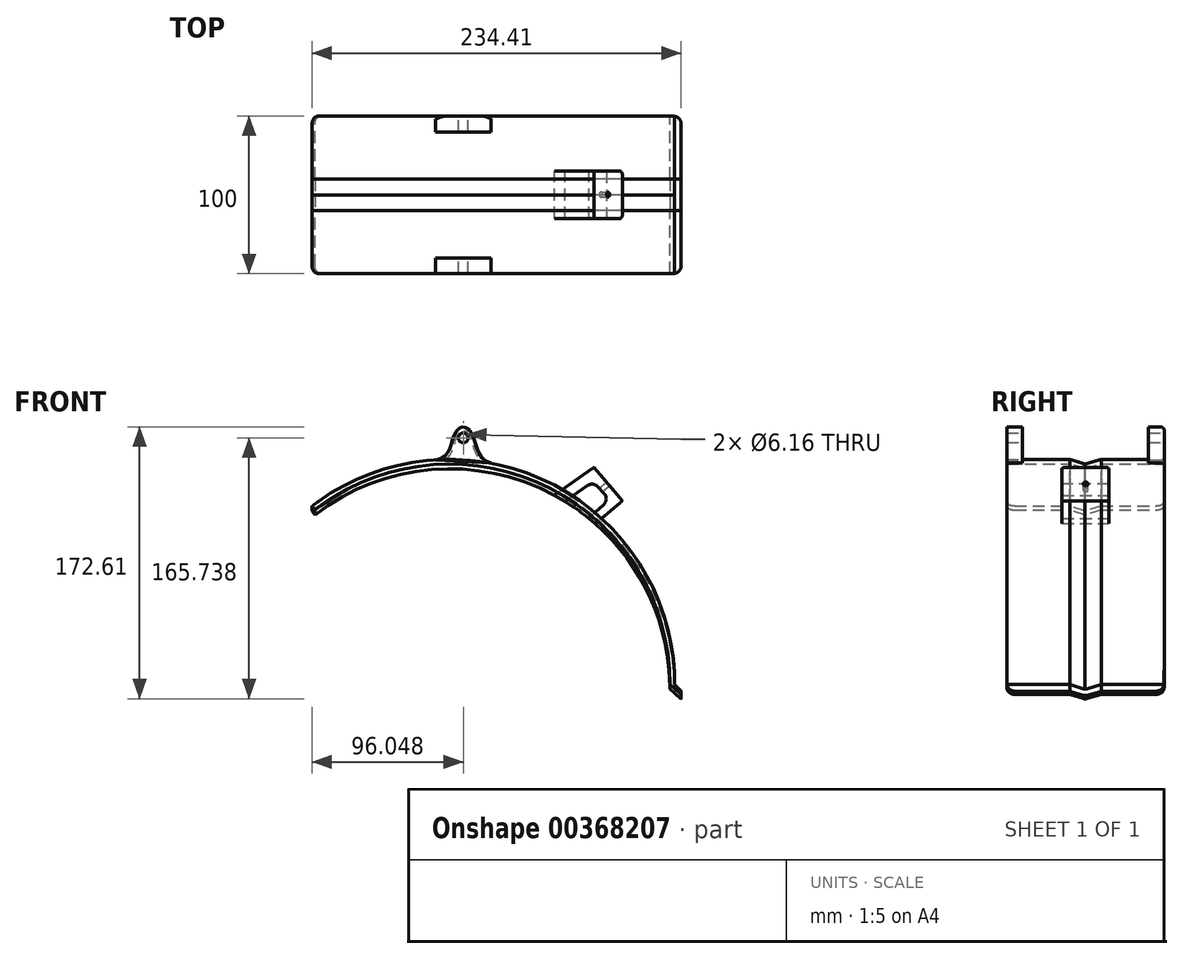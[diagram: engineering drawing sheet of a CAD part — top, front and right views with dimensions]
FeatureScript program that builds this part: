
annotation { "Feature Type Name" : "Feature", "Feature Type Description" : "" }
export const myFeature = defineFeature(function(context is Context, id is Id, definition is map)
    precondition{}
    {
        {
            var Q0;
            Q0=qCreatedBy(makeId("Front.planeOp"),FACE);
            var sketch = newSketch(context, id + "F0", { "sketchPlane" : qUnion([Q0])});
            skArc(sketch, "E0", {"start": v(134.32, 0) * mm, "mid": v(-8.68, 143) * mm, "end": v(-151.68, 0) * mm});
            skArc(sketch, "E1", {"start": v(131.32, 0) * mm, "mid": v(-8.68, 140) * mm, "end": v(-148.68, 0) * mm});
            skLineSegment(sketch, "E2", {"start": v(131.32, 0) * mm, "end": v(134.32, 0) * mm});
            skLineSegment(sketch, "E3", {"start": v(131.32, 0) * mm, "end": v(138.4, -6.25) * mm});
            skLineSegment(sketch, "E4", {"start": v(138.4, -6.25) * mm, "end": v(138.4, -4.25) * mm});
            skLineSegment(sketch, "E5", {"start": v(134.32, 0) * mm, "end": v(138.4, -4.25) * mm});
            skLineSegment(sketch, "E6", {"start": v(-96.01, 113.24) * mm, "end": v(-94.22, 110.83) * mm});
            skSolve(sketch);
        }
        {
            var Q0;
            Q0 = qSketchRegion(id + "F0", true);
            extrude(context, id + "F1", {"entities" : qUnion([Q0]), "depth" : 40 * mm});
        }
        {
            var Q0;
            Q0=qCreatedBy(makeId("Right.planeOp"),FACE);
            var sketch = newSketch(context, id + "F2", { "sketchPlane" : qUnion([Q0])});
            skLineSegment(sketch, "E7", {"start": v(-40, 0) * mm, "end": v(-50.26, -3) * mm});
            skLineSegment(sketch, "E8", {"start": v(-50.26, -3) * mm, "end": v(-60, 0) * mm});
            skSolve(sketch);
        }
        {
            var Q0;
            Q0=makeQuery(id+"F1.opExtrude","CAP_FACE",FACE,{"disambiguationData":[OSD([sQuery(id+"F0.wireOp",EDGE,"E0"),sQuery(id+"F0.wireOp",EDGE,"E1"),sQuery(id+"F0.wireOp",EDGE,"rE3FSKzE-tdSS-Yi37-PZmk-w9ympNAeDIpR"),sQuery(id+"F0.wireOp",EDGE,"E3"),sQuery(id+"F0.wireOp",EDGE,"E4"),sQuery(id+"F0.wireOp",EDGE,"E5")])],"isStart":false});
            var Q1;
            Q1=sQuery(id+"F2.wireOp",EDGE,"E7");
            sweep(context, id + "F3", {"profiles" : qUnion([Q0]), "path" : qUnion([Q1])});
        }
        {
            var Q0;
            Q0=makeQuery(id+"F3.opSweep","CAP_FACE",FACE,{"disambiguationData":[OSD([sQuery(id+"F0.wireOp",EDGE,"E0"),sQuery(id+"F0.wireOp",EDGE,"E1"),sQuery(id+"F0.wireOp",EDGE,"rE3FSKzE-tdSS-Yi37-PZmk-w9ympNAeDIpR"),sQuery(id+"F0.wireOp",EDGE,"E3"),sQuery(id+"F0.wireOp",EDGE,"E4"),sQuery(id+"F0.wireOp",EDGE,"E5"),sQuery(id+"F2.wireOp",VERTEX,"E7.end")])],"isStart":false});
            var Q1;
            Q1=sQuery(id+"F2.wireOp",EDGE,"E8");
            sweep(context, id + "F4", {"operationType" : NewBodyOperationType.ADD, "profiles" : qUnion([Q0]), "path" : qUnion([Q1])});
        }
        {
            var Q0;
            Q0=makeQuery(id+"F4.opSweep","CAP_FACE",FACE,{"disambiguationData":[OSD([sQuery(id+"F0.wireOp",EDGE,"E0"),sQuery(id+"F0.wireOp",EDGE,"E1"),sQuery(id+"F0.wireOp",EDGE,"rE3FSKzE-tdSS-Yi37-PZmk-w9ympNAeDIpR"),sQuery(id+"F0.wireOp",EDGE,"E3"),sQuery(id+"F0.wireOp",EDGE,"E4"),sQuery(id+"F0.wireOp",EDGE,"E5"),sQuery(id+"F2.wireOp",VERTEX,"E7.end"),sQuery(id+"F2.wireOp",VERTEX,"E8.end")])],"isStart":false});
            var Q1;
            Q1 = qSketchRegion(id + "F2", true);
            extrude(context, id + "F5", {"entities" : qUnion([Q0, Q1]), "operationType" : NewBodyOperationType.ADD, "depth" : 40 * mm});
        }
        {
            var Q0;
            Q0=qCreatedBy(makeId("Front.planeOp"),FACE);
            var sketch = newSketch(context, id + "F6", { "sketchPlane" : qUnion([Q0])});
            skFitSpline(sketch, "E9", {"points": [v(-17.5, 142.73) * mm, v(-5.94, 158) * mm, v(0, 163.52) * mm, v(6.18, 157.86) * mm, v(17.58, 140.57) * mm], "startDerivative": vector(93.4, 8.74) * mm, "endDerivative": vector(82.75, -24.1) * mm});
            skLineSegment(sketch, "E10", {"start": v(-17.5, 142.73) * mm, "end": v(17.58, 140.57) * mm});
            skLineSegment(sketch, "E11", {"start": v(0.04, 156.65) * mm, "end": v(0, 141.65) * mm});
            skPoint(sketch, "E11.startSnap0", {"position": v(0.04, 141.65) * mm});
            skCircle(sketch, "E12", {"center": v(0.04, 156.65) * mm, "radius": 3.08 * mm});
            skSolve(sketch);
        }
        {
            var Q0;
            Q0 = qSketchRegion(id + "F6", true);
            extrude(context, id + "F7", {"entities" : qUnion([Q0]), "operationType" : NewBodyOperationType.ADD, "depth" : 10 * mm});
        }
        {
            var Q0;
            Q0 = qSketchRegion(id + "F6", true);
            var Q1;
            Q1=makeQuery(id+"F5.opExtrude","CAP_FACE",FACE,{"disambiguationData":[OSD([sQuery(id+"F0.wireOp",EDGE,"E0"),sQuery(id+"F0.wireOp",EDGE,"E1"),sQuery(id+"F0.wireOp",EDGE,"E3"),sQuery(id+"F0.wireOp",EDGE,"E4"),sQuery(id+"F0.wireOp",EDGE,"E5"),sQuery(id+"F0.wireOp",EDGE,"E6"),sQuery(id+"F2.wireOp",VERTEX,"E7.end"),sQuery(id+"F2.wireOp",VERTEX,"E8.end")])],"isStart":false});
            extrude(context, id + "F8", {"entities" : qUnion([Q0]), "endBound" : BoundingType.UP_TO_SURFACE, "endBoundEntityFace" : qUnion([Q1]), "depth" : 99 * mm, "hasSecondDirection" : true, "secondDirectionOppositeDirection" : false, "secondDirectionDepth" : 90 * mm});
        }
        {
            var Q0;
            Q0=qCreatedBy(makeId("Front.planeOp"),FACE);
            var sketch = newSketch(context, id + "F9", { "sketchPlane" : qUnion([Q0])});
            skLineSegment(sketch, "E13", {"start": v(57.91, 120.15) * mm, "end": v(83.18, 137.94) * mm});
            skLineSegment(sketch, "E14", {"start": v(83.18, 137.94) * mm, "end": v(101.02, 116.66) * mm});
            skLineSegment(sketch, "E15", {"start": v(101.02, 116.66) * mm, "end": v(83.72, 102.17) * mm});
            skLineSegment(sketch, "E16", {"start": v(64.64, 116.26) * mm, "end": v(82.45, 128.8) * mm});
            skLineSegment(sketch, "E17", {"start": v(82.45, 128.8) * mm, "end": v(92.9, 117.86) * mm});
            skLineSegment(sketch, "E18", {"start": v(92.9, 117.86) * mm, "end": v(79.89, 105.42) * mm});
            skLineSegment(sketch, "E19", {"start": v(57.91, 120.15) * mm, "end": v(64.64, 116.26) * mm});
            skLineSegment(sketch, "E20", {"start": v(79.89, 105.42) * mm, "end": v(83.72, 102.17) * mm});
            skSolve(sketch);
        }
        {
            var Q0;
            Q0 = qSketchRegion(id + "F9", true);
            extrude(context, id + "F10", {"entities" : qUnion([Q0]), "depth" : 65 * mm, "hasSecondDirection" : true, "secondDirectionOppositeDirection" : false, "secondDirectionDepth" : 35 * mm});
        }
        {
            var Q0;
            Q0=makeQuery(id+"F10.opExtrude","CAP_EDGE",EDGE,{"disambiguationData":[OSD([sQuery(id+"F9.wireOp",EDGE,"E14")])],"isStart":false});
            var Q1;
            Q1=makeQuery(id+"F10.opExtrude","CAP_EDGE",EDGE,{"disambiguationData":[OSD([sQuery(id+"F9.wireOp",EDGE,"E14")])],"isStart":true});
            var Q2;
            Q2=makeQuery(id+"F7.opExtrude","CAP_EDGE",EDGE,{"disambiguationData":[OSD([sQuery(id+"F6.wireOp",EDGE,"E9")])],"isStart":true});
            var Q3;
            Q3=makeQuery(id+"F8.opExtrude","TWEAK_EDGE",EDGE,{"derivedFrom":[makeQuery(id+"F5.opExtrude","CAP_FACE",FACE,{"disambiguationData":[OSD([sQuery(id+"F0.wireOp",EDGE,"E0"),sQuery(id+"F0.wireOp",EDGE,"E1"),sQuery(id+"F0.wireOp",EDGE,"E3"),sQuery(id+"F0.wireOp",EDGE,"E4"),sQuery(id+"F0.wireOp",EDGE,"E5"),sQuery(id+"F0.wireOp",EDGE,"E6"),sQuery(id+"F2.wireOp",VERTEX,"E7.end"),sQuery(id+"F2.wireOp",VERTEX,"E8.end")])],"isStart":false}),makeQuery(id+"F6.imprint","IMPRINT",EDGE,{"derivedFrom":sQuery(id+"F6.wireOp",EDGE,"E9")})]});
            fillet(context, id + "F11", {"entities" : qUnion([Q0, Q1, Q2, Q3]), "radius" : 2 * mm, "tangentPropagation" : true, "allowEdgeOverflow" : false});
        }
        {
            var Q0;
            Q0=makeQuery(id+"F5.opExtrude","CAP_EDGE",EDGE,{"disambiguationData":[OSD([sQuery(id+"F0.wireOp",EDGE,"E4"),sQuery(id+"F2.wireOp",VERTEX,"E7.end"),sQuery(id+"F2.wireOp",VERTEX,"E8.end")])],"isStart":false});
            var Q1;
            Q1=makeQuery(id+"F1.opExtrude","CAP_EDGE",EDGE,{"disambiguationData":[OSD([sQuery(id+"F0.wireOp",EDGE,"E4")])],"isStart":true});
            var Q2;
            {var subQ0=sQuery(id+"F2.wireOp",VERTEX,"E7.end");var subQ1=sQuery(id+"F0.wireOp",EDGE,"E3");Q2=makeQuery(id+"F4.boolean.opBoolean","MERGE",EDGE,{"derivedFrom":[makeQuery(id+"F3.opSweep","CAP_EDGE",EDGE,{"disambiguationData":[OSD([subQ1,subQ0])],"isStart":false}),makeQuery(id+"F4.opSweep","CAP_EDGE",EDGE,{"disambiguationData":[OSD([subQ1,subQ0,sQuery(id+"F2.wireOp",VERTEX,"E8.start")])],"isStart":true})]});}
            var Q3;
            {var subQ0=sQuery(id+"F2.wireOp",VERTEX,"E7.end");var subQ1=sQuery(id+"F0.wireOp",EDGE,"E5");Q3=makeQuery(id+"F4.boolean.opBoolean","MERGE",EDGE,{"derivedFrom":[makeQuery(id+"F3.opSweep","CAP_EDGE",EDGE,{"disambiguationData":[OSD([subQ1,subQ0])],"isStart":false}),makeQuery(id+"F4.opSweep","CAP_EDGE",EDGE,{"disambiguationData":[OSD([subQ1,subQ0,sQuery(id+"F2.wireOp",VERTEX,"E8.start")])],"isStart":true})]});}
            var Q4;
            Q4=makeQuery(id+"F1.opExtrude","CAP_EDGE",EDGE,{"disambiguationData":[OSD([sQuery(id+"F0.wireOp",EDGE,"E6")])],"isStart":true});
            var Q5;
            Q5=makeQuery(id+"F5.opExtrude","CAP_EDGE",EDGE,{"disambiguationData":[OSD([sQuery(id+"F0.wireOp",EDGE,"E6"),sQuery(id+"F2.wireOp",VERTEX,"E7.end"),sQuery(id+"F2.wireOp",VERTEX,"E8.end")])],"isStart":false});
            fillet(context, id + "F12", {"entities" : qUnion([Q0, Q1, Q2, Q3, Q4, Q5]), "radius" : 5 * mm, "tangentPropagation" : true, "allowEdgeOverflow" : false});
        }
        {
            var Q0;
            Q0=makeQuery(id+"F10.opExtrude","SWEPT_EDGE",EDGE,{"disambiguationData":[OSD([sQuery(id+"F9.wireOp",EDGE,"E16"),sQuery(id+"F9.wireOp",EDGE,"E17")])]});
            var Q1;
            Q1=makeQuery(id+"F10.opExtrude","SWEPT_EDGE",EDGE,{"disambiguationData":[OSD([sQuery(id+"F9.wireOp",EDGE,"E17"),sQuery(id+"F9.wireOp",EDGE,"E18")])]});
            fillet(context, id + "F13", {"entities" : qUnion([Q0, Q1]), "radius" : 5 * mm, "tangentPropagation" : true, "allowEdgeOverflow" : false});
        }
        {
            var Q0;
            Q0=makeQuery(id+"F10.opExtrude","SWEPT_FACE",FACE,{"disambiguationData":[OSD([sQuery(id+"F9.wireOp",EDGE,"E14")])]});
            cPlane(context, id + "F14", {"entities" : qUnion([Q0]), "cplaneType" : CPlaneType.OFFSET, "offset" : 0 * mm, "width" : 150 * mm, "height" : 150 * mm});
        }
        {
            var Q0;
            Q0=qCreatedBy(id+"F14.planeOp",FACE);
            var sketch = newSketch(context, id + "F15", { "sketchPlane" : qUnion([Q0])});
            skCircle(sketch, "E21", {"center": v(-49.85, 38.53) * mm, "radius": 1.5 * mm});
            skSolve(sketch);
        }
        {
            var Q0;
            Q0=sQuery(id+"F15.wireOp",VERTEX,"E21.center");
            var Q1;
            Q1=makeQuery(id+"F10.opExtrude","SWEPT_BODY",BODY,{"disambiguationData":[OSD([sQuery(id+"F9.wireOp",EDGE,"E13"),sQuery(id+"F9.wireOp",EDGE,"E14"),sQuery(id+"F9.wireOp",EDGE,"E15"),sQuery(id+"F9.wireOp",EDGE,"E16"),sQuery(id+"F9.wireOp",EDGE,"E17"),sQuery(id+"F9.wireOp",EDGE,"E18"),sQuery(id+"F9.wireOp",EDGE,"E19"),sQuery(id+"F9.wireOp",EDGE,"E20")])]});
            hole(context, id + "F16", {"style" : HoleStyle.SIMPLE, "endStyle" : HoleEndStyle.THROUGH, "holeDiameter" : 3 * mm, "isTappedThrough" : true, "tappedDepth" : 12 * mm, "tapClearance" : 3, "locations" : qUnion([Q0]), "scope" : qUnion([Q1])});
        }
    });
